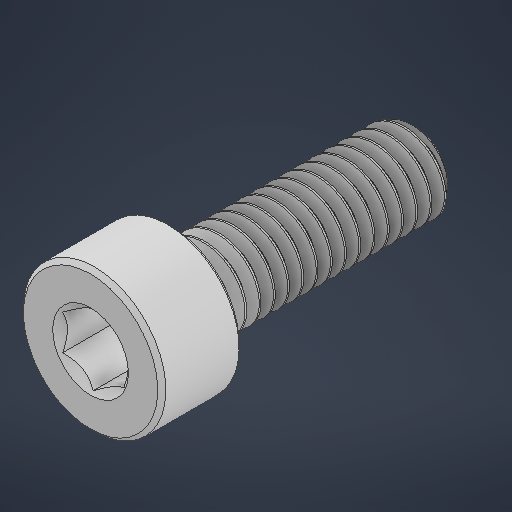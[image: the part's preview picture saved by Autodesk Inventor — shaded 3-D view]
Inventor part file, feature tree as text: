
AUTODESK INVENTOR PART (.ipt)
format: ipt  version: 2025 (Build 290162000, 162)  size: 600,064 bytes
history: native  units: in
note: dims shown in document units (in); Inventor stores cm internally (conversion verified against a paired STEP export)
features: revolve x1
ambient origin geometry x8: Origin, YZ Plane, XZ Plane, XY Plane, X Axis, Y Axis, Z Axis, Center Point
bodies: Solid1 (feature_tree)
feature tree (1):
  revolve  "Revolve2"  [1 undecoded]
note: 1 required parameter value undecoded (feature->parameter linkage not recoverable at this tier; creation-order binding heuristic only, values carry confidence <= 0.55)
